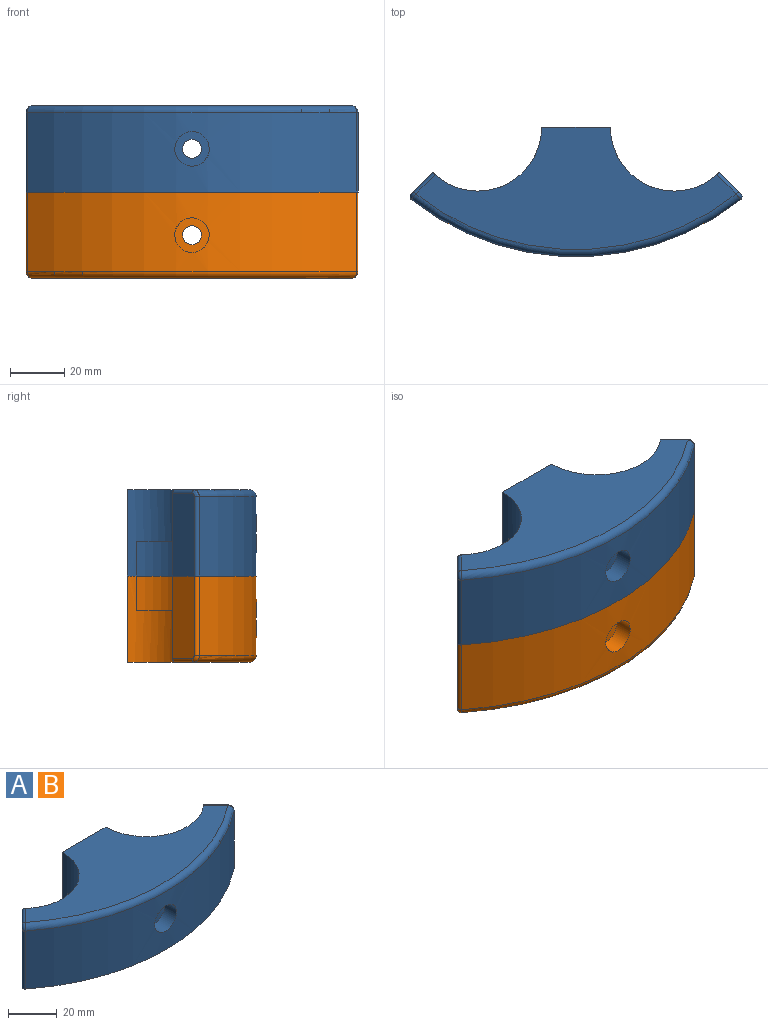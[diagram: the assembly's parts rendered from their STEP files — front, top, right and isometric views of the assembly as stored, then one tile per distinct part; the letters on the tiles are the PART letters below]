
ASSEMBLY  parts=2 mates=1
PART A: 26 faces, bbox 131.4x55.6x31.8 mm
  f0: cylinder r=6.35mm len=12.7mm, axis (0,1,0), area 272.2mm2, adj f4,f25
  f1: cylinder r=23.49mm len=40.11mm, axis (0,0,-1), area 1135.1mm2, adj f3,f6,f7,f8,f13,f20,f22,f23
  f2: cylinder r=23.49mm len=40.11mm, axis (0,0,-1), area 1135.1mm2, adj f5,f6,f7,f8,f10,f17,f18,f19
  f3: plane 30.48x7.98mm, normal (-0.71,0.71,0), area 343.6mm2, adj f1,f8,f13,f14,f15
  f4: cylinder r=97.86mm len=121.35mm, axis (0,0,-1), area 3696.7mm2, adj f0,f8,f9,f12,f15
  f5: plane 30.48x7.98mm, normal (0.71,0.71,0), area 343.6mm2, adj f2,f8,f10,f11,f12
  f6: plane 31.75x25.4mm, normal (0,1,0), area 768.1mm2, adj f1,f2,f7,f8,f24
  f7: plane 117.97x45.03mm, normal (0,0,1), area 2702mm2, adj f1,f2,f6,f9,f10,f13
  f8: plane 122.32x47.57mm, normal (0,0,-1), area 2797.3mm2, adj f1,f2,f3,f4,f5,f6,f12,f15
  f9: torus R=95.32mm, axis (0,0,1), area 516.7mm2, adj f4,f7,f11,f14
  f10: cylinder r=1.27mm len=8mm, axis (0.71,-0.71,0), area 20mm2, adj f2,f5,f7,f11
  f11: bspline ~3.2x3.19mm, area 6.9mm2, adj f5,f9,f10,f12
  f12: cylinder r=1.27mm len=29.21mm, axis (0,0,-1), area 62.6mm2, adj f4,f5,f8,f11
  f13: cylinder r=1.27mm len=8mm, axis (0.71,0.71,0), area 20mm2, adj f1,f3,f7,f14
  f14: bspline ~3.2x3.19mm, area 6.9mm2, adj f3,f9,f13,f15
  f15: cylinder r=1.27mm len=29.21mm, axis (0,0,-1), area 62.6mm2, adj f3,f4,f8,f14
  f16: cylinder r=26.04mm len=41.87mm, axis (0,0,-1), area 698.2mm2, adj f8,f17,f18,f19
  f17: plane 12.7x2.56mm, normal (0,-1,0), area 32.5mm2, adj f2,f8,f16,f19
  f18: plane 12.7x1.81mm, normal (-0.71,-0.71,0), area 32.5mm2, adj f2,f8,f16,f19
  f19: plane 41.87x22.86mm, normal (0,0,-1), area 132mm2, adj f2,f16,f17,f18
  f20: plane 12.7x2.56mm, normal (0,-1,0), area 32.5mm2, adj f1,f8,f21,f23
  f21: cylinder r=26.04mm len=41.87mm, axis (0,0,-1), area 698.2mm2, adj f8,f20,f22,f23
  f22: plane 12.7x1.81mm, normal (0.71,-0.71,0), area 32.5mm2, adj f1,f8,f21,f23
  f23: plane 41.87x22.86mm, normal (0,0,-1), area 132mm2, adj f1,f20,f21,f22
  f24: cylinder r=3.49mm len=40.64mm, axis (0,1,0), area 891.8mm2, adj f6,f25
  f25: plane 12.7x12.7mm, normal (0,-1,0), area 88.4mm2, adj f0,f24
PART B: same geometry as A
PLACE A at identity
PLACE B rot(axis=(0,1,0),180deg) t=(-13.28,0,0)mm
MATE planar B.f8 <-> A.f8  axis (0,0,1) through (-6.64,-8.22,0)mm
